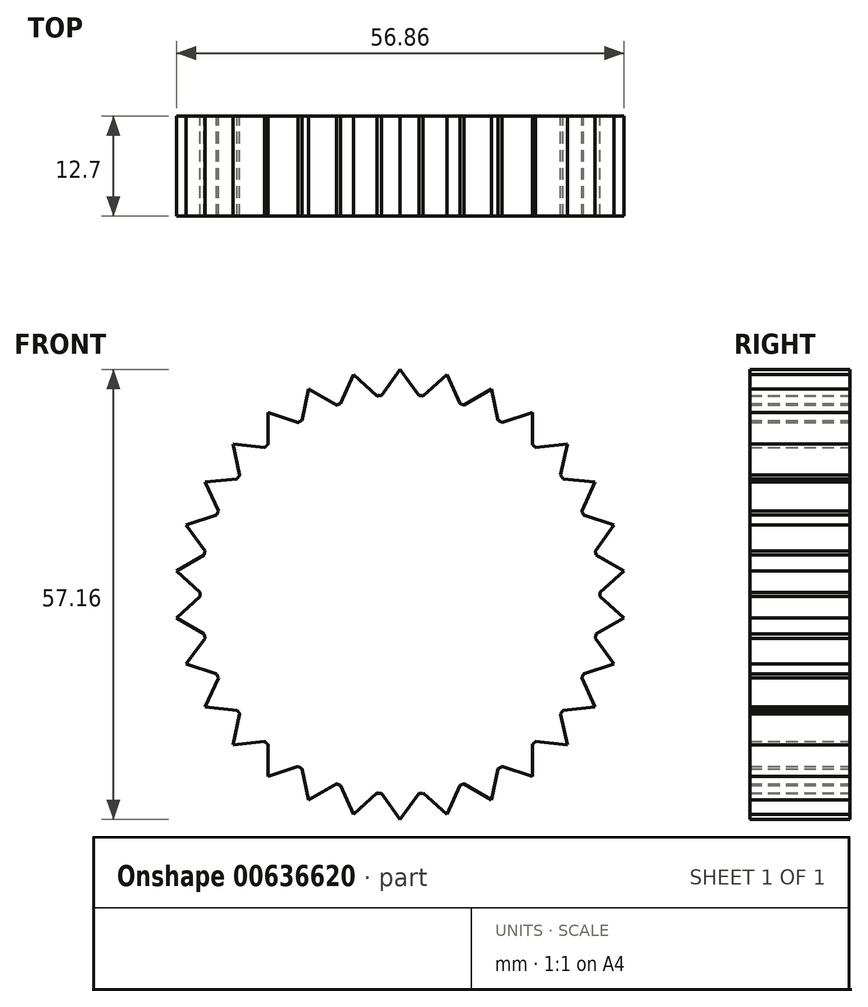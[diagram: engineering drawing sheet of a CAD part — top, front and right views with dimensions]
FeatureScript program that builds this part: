
annotation { "Feature Type Name" : "Feature", "Feature Type Description" : "" }
export const myFeature = defineFeature(function(context is Context, id is Id, definition is map)
    precondition{}
    {
        {
            var Q0;
            Q0=qCreatedBy(makeId("Front.planeOp"),FACE);
            var sketch = newSketch(context, id + "F0", { "sketchPlane" : qUnion([Q0])});
            skCircle(sketch, "E0", {"center": v(0, 0) * mm, "radius": 25.4 * mm});
            skLineSegment(sketch, "E1", {"start": v(0, 25.4) * mm, "end": v(0, 28.58) * mm, "construction": true});
            skLineSegment(sketch, "E2", {"start": v(0, 28.58) * mm, "end": v(-2.38, 25.29) * mm});
            skLineSegment(sketch, "E3.MirrorCS", {"start": v(0, 28.58) * mm, "end": v(2.38, 25.29) * mm});
            skLineSegment(sketch, "E4.1.0", {"start": v(-5.94, 27.96) * mm, "end": v(-7.58, 24.24) * mm});
            skLineSegment(sketch, "E4.1.1", {"start": v(-5.94, 27.96) * mm, "end": v(-2.93, 25.23) * mm});
            skLineSegment(sketch, "E4.2.0", {"start": v(-11.63, 26.11) * mm, "end": v(-12.46, 22.13) * mm});
            skLineSegment(sketch, "E4.2.1", {"start": v(-11.63, 26.11) * mm, "end": v(-8.11, 24.07) * mm});
            skLineSegment(sketch, "E4.3.0", {"start": v(-16.8, 23.13) * mm, "end": v(-16.79, 19.06) * mm});
            skLineSegment(sketch, "E4.3.1", {"start": v(-16.8, 23.13) * mm, "end": v(-12.94, 21.86) * mm});
            skLineSegment(sketch, "E4.4.0", {"start": v(-21.24, 19.13) * mm, "end": v(-20.38, 15.15) * mm});
            skLineSegment(sketch, "E4.4.1", {"start": v(-21.24, 19.13) * mm, "end": v(-17.2, 18.69) * mm});
            skLineSegment(sketch, "E4.5.0", {"start": v(-24.75, 14.3) * mm, "end": v(-23.09, 10.58) * mm});
            skLineSegment(sketch, "E4.5.1", {"start": v(-24.75, 14.3) * mm, "end": v(-20.71, 14.7) * mm});
            skLineSegment(sketch, "E4.6.0", {"start": v(-27.19, 8.83) * mm, "end": v(-24.79, 5.55) * mm});
            skLineSegment(sketch, "E4.6.1", {"start": v(-27.19, 8.83) * mm, "end": v(-23.32, 10.08) * mm});
            skLineSegment(sketch, "E4.7.0", {"start": v(-28.43, 2.99) * mm, "end": v(-25.4, 0.28) * mm});
            skLineSegment(sketch, "E4.7.1", {"start": v(-28.43, 2.99) * mm, "end": v(-24.9, 5) * mm});
            skLineSegment(sketch, "E4.8.0", {"start": v(-28.43, -2.99) * mm, "end": v(-24.9, -5) * mm});
            skLineSegment(sketch, "E4.8.1", {"start": v(-28.43, -2.99) * mm, "end": v(-25.4, -0.28) * mm});
            skLineSegment(sketch, "E4.9.0", {"start": v(-27.19, -8.83) * mm, "end": v(-23.32, -10.08) * mm});
            skLineSegment(sketch, "E4.9.1", {"start": v(-27.19, -8.83) * mm, "end": v(-24.79, -5.55) * mm});
            skLineSegment(sketch, "E4.10.0", {"start": v(-24.75, -14.3) * mm, "end": v(-20.71, -14.7) * mm});
            skLineSegment(sketch, "E4.10.1", {"start": v(-24.75, -14.3) * mm, "end": v(-23.09, -10.58) * mm});
            skLineSegment(sketch, "E4.11.0", {"start": v(-21.24, -19.13) * mm, "end": v(-17.2, -18.69) * mm});
            skLineSegment(sketch, "E4.11.1", {"start": v(-21.24, -19.13) * mm, "end": v(-20.38, -15.15) * mm});
            skLineSegment(sketch, "E4.12.0", {"start": v(-16.8, -23.13) * mm, "end": v(-12.94, -21.86) * mm});
            skLineSegment(sketch, "E4.12.1", {"start": v(-16.8, -23.13) * mm, "end": v(-16.79, -19.06) * mm});
            skLineSegment(sketch, "E4.13.0", {"start": v(-11.63, -26.11) * mm, "end": v(-8.11, -24.07) * mm});
            skLineSegment(sketch, "E4.13.1", {"start": v(-11.63, -26.11) * mm, "end": v(-12.46, -22.13) * mm});
            skLineSegment(sketch, "E4.14.0", {"start": v(-5.94, -27.96) * mm, "end": v(-2.93, -25.23) * mm});
            skLineSegment(sketch, "E4.14.1", {"start": v(-5.94, -27.96) * mm, "end": v(-7.58, -24.24) * mm});
            skLineSegment(sketch, "E4.15.0", {"start": v(0, -28.58) * mm, "end": v(2.38, -25.29) * mm});
            skLineSegment(sketch, "E4.15.1", {"start": v(0, -28.58) * mm, "end": v(-2.38, -25.29) * mm});
            skLineSegment(sketch, "E4.16.0", {"start": v(5.94, -27.96) * mm, "end": v(7.58, -24.24) * mm});
            skLineSegment(sketch, "E4.16.1", {"start": v(5.94, -27.96) * mm, "end": v(2.93, -25.23) * mm});
            skLineSegment(sketch, "E4.17.0", {"start": v(11.63, -26.11) * mm, "end": v(12.46, -22.13) * mm});
            skLineSegment(sketch, "E4.17.1", {"start": v(11.63, -26.11) * mm, "end": v(8.11, -24.07) * mm});
            skLineSegment(sketch, "E4.18.0", {"start": v(16.8, -23.13) * mm, "end": v(16.79, -19.06) * mm});
            skLineSegment(sketch, "E4.18.1", {"start": v(16.8, -23.13) * mm, "end": v(12.94, -21.86) * mm});
            skLineSegment(sketch, "E4.19.0", {"start": v(21.24, -19.13) * mm, "end": v(20.38, -15.15) * mm});
            skLineSegment(sketch, "E4.19.1", {"start": v(21.24, -19.13) * mm, "end": v(17.2, -18.69) * mm});
            skLineSegment(sketch, "E4.20.0", {"start": v(24.75, -14.3) * mm, "end": v(23.09, -10.58) * mm});
            skLineSegment(sketch, "E4.20.1", {"start": v(24.75, -14.3) * mm, "end": v(20.71, -14.7) * mm});
            skLineSegment(sketch, "E4.21.0", {"start": v(27.19, -8.83) * mm, "end": v(24.79, -5.55) * mm});
            skLineSegment(sketch, "E4.21.1", {"start": v(27.19, -8.83) * mm, "end": v(23.32, -10.08) * mm});
            skLineSegment(sketch, "E4.22.0", {"start": v(28.43, -2.99) * mm, "end": v(25.4, -0.28) * mm});
            skLineSegment(sketch, "E4.22.1", {"start": v(28.43, -2.99) * mm, "end": v(24.9, -5) * mm});
            skLineSegment(sketch, "E4.23.0", {"start": v(28.43, 2.99) * mm, "end": v(24.9, 5) * mm});
            skLineSegment(sketch, "E4.23.1", {"start": v(28.43, 2.99) * mm, "end": v(25.4, 0.28) * mm});
            skLineSegment(sketch, "E4.24.0", {"start": v(27.19, 8.83) * mm, "end": v(23.32, 10.08) * mm});
            skLineSegment(sketch, "E4.24.1", {"start": v(27.19, 8.83) * mm, "end": v(24.79, 5.55) * mm});
            skLineSegment(sketch, "E4.25.0", {"start": v(24.75, 14.3) * mm, "end": v(20.71, 14.7) * mm});
            skLineSegment(sketch, "E4.25.1", {"start": v(24.75, 14.3) * mm, "end": v(23.09, 10.58) * mm});
            skLineSegment(sketch, "E4.26.0", {"start": v(21.24, 19.13) * mm, "end": v(17.2, 18.69) * mm});
            skLineSegment(sketch, "E4.26.1", {"start": v(21.24, 19.13) * mm, "end": v(20.38, 15.15) * mm});
            skLineSegment(sketch, "E4.27.0", {"start": v(16.8, 23.13) * mm, "end": v(12.94, 21.86) * mm});
            skLineSegment(sketch, "E4.27.1", {"start": v(16.8, 23.13) * mm, "end": v(16.79, 19.06) * mm});
            skLineSegment(sketch, "E4.28.0", {"start": v(11.63, 26.11) * mm, "end": v(8.11, 24.07) * mm});
            skLineSegment(sketch, "E4.28.1", {"start": v(11.63, 26.11) * mm, "end": v(12.46, 22.13) * mm});
            skLineSegment(sketch, "E4.29.0", {"start": v(5.94, 27.96) * mm, "end": v(2.93, 25.23) * mm});
            skLineSegment(sketch, "E4.29.1", {"start": v(5.94, 27.96) * mm, "end": v(7.58, 24.24) * mm});
            skSolve(sketch);
        }
        {
            var Q0;
            Q0 = qSketchRegion(id + "F0", true);
            extrude(context, id + "F1", {"entities" : qUnion([Q0]), "depth" : 12.7 * mm, "offsetDistance" : 25.4 * mm});
        }
    });
